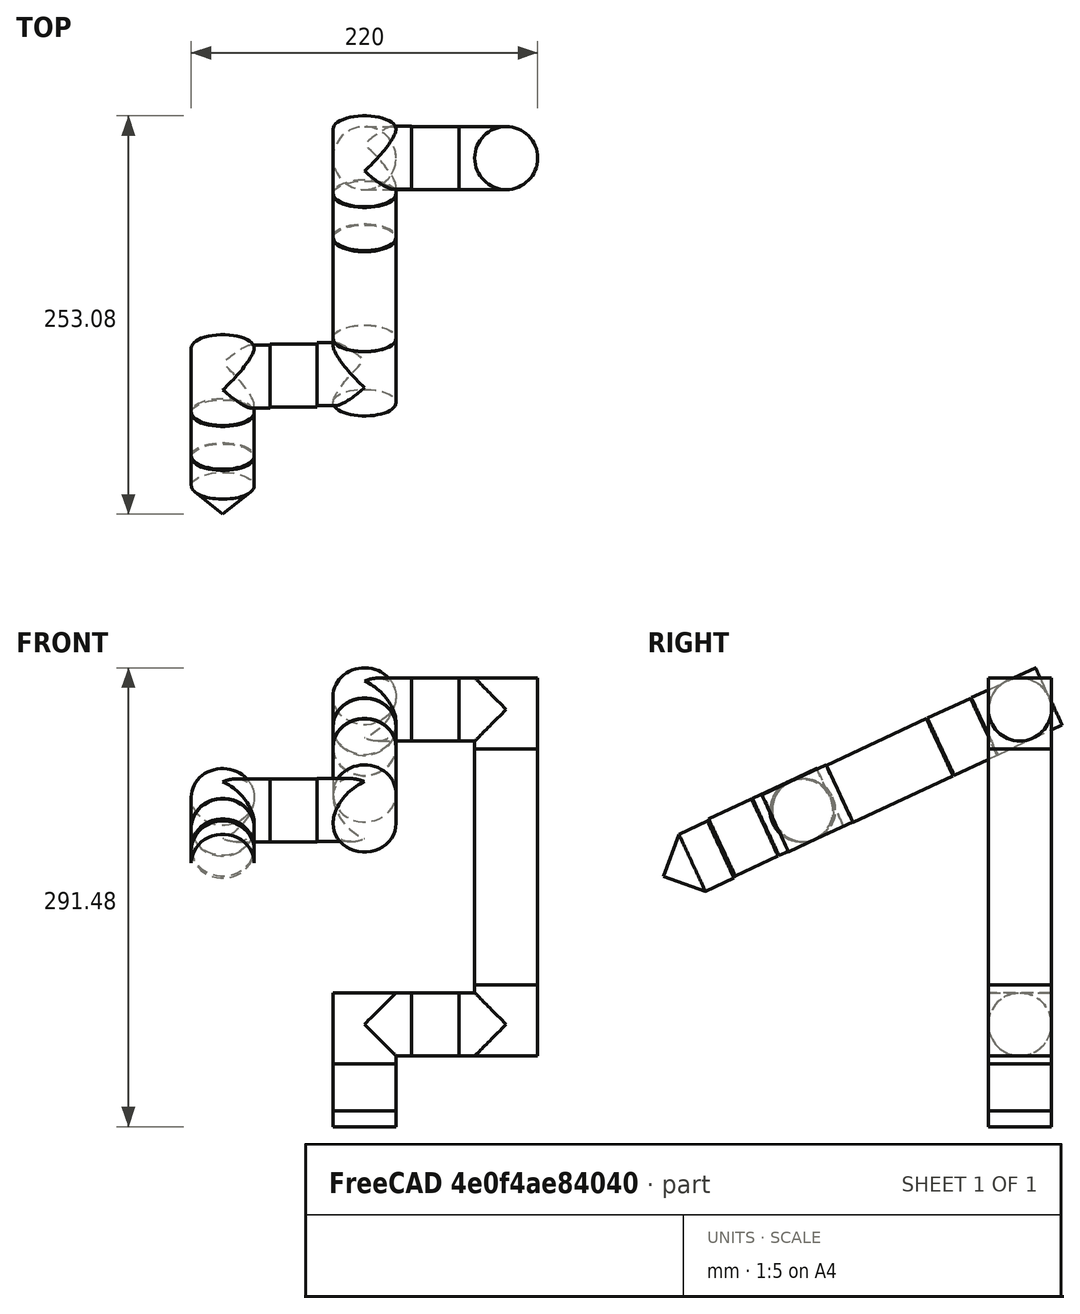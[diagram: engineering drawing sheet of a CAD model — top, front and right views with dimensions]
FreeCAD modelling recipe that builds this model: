
FCSTD DOCUMENT  (FreeCAD 0.17R7965 (Git))
Label: arbot-block
License: All rights reserved
LicenseURL: http://en.wikipedia.org/wiki/All_rights_reserved
objects: Part::Cylinder×22, Part::FeaturePython×6, Part::Chamfer×1
note: 29 computed .brp shape members not serialized (recipe doc carries the construction recipe); baked Part::Feature solids carry a one-line shape summary decoded from their .brp

FEATURE [Part::Cylinder] Cylinder001
  Angle = 360
  AttacherType = Attacher::AttachEngine3D
  Height = 30
  Placement = pos=(0,0,40) rot=(0,1,0;1.5708rad)
  Radius = 20
FEATURE [Part::Cylinder] Cylinder002
  Angle = 360
  AttacherType = Attacher::AttachEngine3D
  Height = 40
  Placement = pos=(-90,-190,166) rot=(1,0,0;2.00713rad)
  Radius = 20
FEATURE [Part::Cylinder] Cylinder003
  Angle = 360
  AttacherType = Attacher::AttachEngine3D
  Height = 45
  Placement = pos=(0,0,15) rot=(0,0,1;0rad)
  Radius = 20
FEATURE [Part::FeaturePython] Connect  # WARN: FeaturePython — macro-defined, semantics opaque (R4)
  Base = -> Cylinder001
  Mode = 1
  Placement = pos=(0,0,15) rot=(0,0,1;0rad)
  Tool = -> Cylinder003
FEATURE [Part::Cylinder] Cylinder004
  Angle = 360
  AttacherType = Attacher::AttachEngine3D
  Height = 30
  Placement = pos=(30,0,255) rot=(0,1,0;1.5708rad)
  Radius = 20
FEATURE [Part::Cylinder] Cylinder005
  Angle = 360
  AttacherType = Attacher::AttachEngine3D
  Height = 30
  Placement = pos=(-90,-162,180) rot=(1,0,0;2.00713rad)
  Radius = 20
FEATURE [Part::Cylinder] Cylinder006
  Angle = 360
  AttacherType = Attacher::AttachEngine3D
  Height = 30
  Placement = pos=(0,0,40) rot=(0,1,0;1.5708rad)
  Radius = 20
FEATURE [Part::Cylinder] Cylinder007
  Angle = 360
  AttacherType = Attacher::AttachEngine3D
  Height = 45
  Placement = pos=(0,0,15) rot=(0,0,1;0rad)
  Radius = 20
FEATURE [Part::FeaturePython] Connect001  # WARN: FeaturePython — macro-defined, semantics opaque (R4)
  Base = -> Cylinder006
  Mode = 1
  Placement = pos=(0,-101,208) rot=(0,0.843661,-0.536875;3.14159rad)
  Tool = -> Cylinder007
FEATURE [Part::Cylinder] Cylinder008
  Angle = 360
  AttacherType = Attacher::AttachEngine3D
  Height = 10
  Placement = pos=(0,0,-10) rot=(0,0,1;0rad)
  Radius = 20
FEATURE [Part::Cylinder] Cylinder009
  Angle = 360
  AttacherType = Attacher::AttachEngine3D
  Height = 30
  Placement = pos=(0,0,40) rot=(0,1,0;1.5708rad)
  Radius = 20
FEATURE [Part::Cylinder] Cylinder010
  Angle = 360
  AttacherType = Attacher::AttachEngine3D
  Height = 45
  Placement = pos=(0,0,15) rot=(0,0,1;0rad)
  Radius = 20
FEATURE [Part::FeaturePython] Connect002  # WARN: FeaturePython — macro-defined, semantics opaque (R4)
  Base = -> Cylinder009
  Mode = 1
  Placement = pos=(-90,-175,174) rot=(-1,0,0;1.13446rad)
  Tool = -> Cylinder010
FEATURE [Part::Cylinder] Cylinder011
  Angle = 360
  AttacherType = Attacher::AttachEngine3D
  Height = 30
  Placement = pos=(-60,-138,191) rot=(0,1,0;1.5708rad)
  Radius = 20
FEATURE [Part::Cylinder] Cylinder012
  Angle = 360
  AttacherType = Attacher::AttachEngine3D
  Height = 30
  Placement = pos=(0,0,40) rot=(0,1,0;1.5708rad)
  Radius = 20
FEATURE [Part::Cylinder] Cylinder013
  Angle = 360
  AttacherType = Attacher::AttachEngine3D
  Height = 45
  Placement = pos=(0,0,15) rot=(0,0,1;0rad)
  Radius = 20
FEATURE [Part::FeaturePython] Connect003  # WARN: FeaturePython — macro-defined, semantics opaque (R4)
  Base = -> Cylinder012
  Mode = 1
  Placement = pos=(90,0,215) rot=(0,0,1;3.14159rad)
  Tool = -> Cylinder013
FEATURE [Part::Cylinder] Cylinder014
  Angle = 360
  AttacherType = Attacher::AttachEngine3D
  Height = 30
  Radius = 20
FEATURE [Part::Cylinder] Cylinder015
  Angle = 360
  AttacherType = Attacher::AttachEngine3D
  Height = 150
  Placement = pos=(90,0,80) rot=(0,0,1;0rad)
  Radius = 20
FEATURE [Part::Cylinder] Cylinder016
  Angle = 360
  AttacherType = Attacher::AttachEngine3D
  Height = 30
  Placement = pos=(0,0,40) rot=(0,1,0;1.5708rad)
  Radius = 20
FEATURE [Part::Cylinder] Cylinder017
  Angle = 360
  AttacherType = Attacher::AttachEngine3D
  Height = 45
  Placement = pos=(0,0,15) rot=(0,0,1;0rad)
  Radius = 20
FEATURE [Part::FeaturePython] Connect004  # WARN: FeaturePython — macro-defined, semantics opaque (R4)
  Base = -> Cylinder016
  Mode = 1
  Placement = pos=(90,0,95) rot=(0,1,0;3.14159rad)
  Tool = -> Cylinder017
FEATURE [Part::Cylinder] Cylinder018
  Angle = 360
  AttacherType = Attacher::AttachEngine3D
  Height = 30
  Placement = pos=(30,0,55) rot=(0,1,0;1.5708rad)
  Radius = 20
FEATURE [Part::Cylinder] Cylinder019
  Angle = 360
  AttacherType = Attacher::AttachEngine3D
  Height = 30
  Placement = pos=(0,0,40) rot=(0,1,0;1.5708rad)
  Radius = 20
FEATURE [Part::Cylinder] Cylinder020
  Angle = 360
  AttacherType = Attacher::AttachEngine3D
  Height = 45
  Placement = pos=(0,0,15) rot=(0,0,1;0rad)
  Radius = 20
FEATURE [Part::FeaturePython] Connect005  # WARN: FeaturePython — macro-defined, semantics opaque (R4)
  Base = -> Cylinder019
  Mode = 1
  Placement = pos=(0,-36,238) rot=(-1,0,0;1.13446rad)
  Tool = -> Cylinder020
FEATURE [Part::Cylinder] Cylinder021
  Angle = 360
  AttacherType = Attacher::AttachEngine3D
  Height = 30
  Placement = pos=(0,-23,244) rot=(1,0,0;2.00713rad)
  Radius = 20
FEATURE [Part::Cylinder] Cylinder022
  Angle = 360
  AttacherType = Attacher::AttachEngine3D
  Height = 70
  Placement = pos=(0,-51,231) rot=(1,0,0;2.00713rad)
  Radius = 20
FEATURE [Part::Chamfer] Chamfer
  Base = -> Cylinder002
  Edges = 1 edges: [Edge1 r1=10 r2=40]
